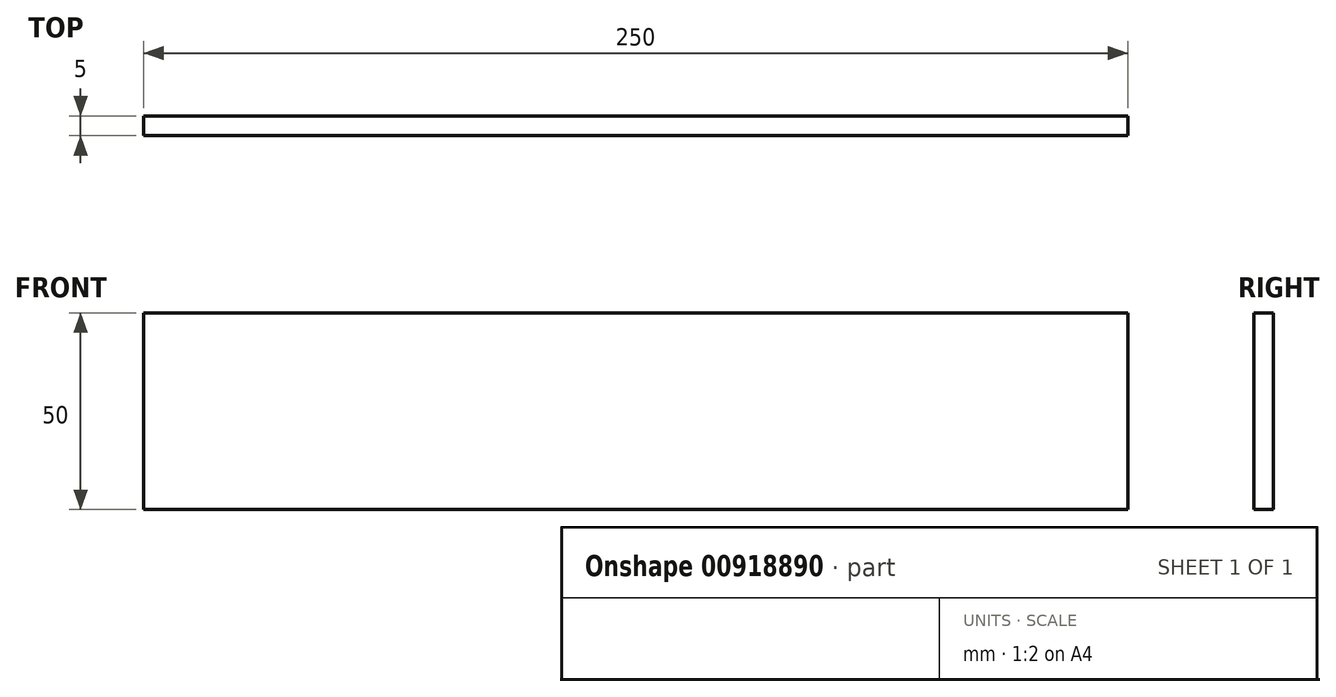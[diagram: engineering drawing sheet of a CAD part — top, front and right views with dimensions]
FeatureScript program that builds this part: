
annotation { "Feature Type Name" : "Feature", "Feature Type Description" : "" }
export const myFeature = defineFeature(function(context is Context, id is Id, definition is map)
    precondition{}
    {
        {
            var Q0;
            Q0=qCreatedBy(makeId("Front.planeOp"),FACE);
            var sketch = newSketch(context, id + "F0", { "sketchPlane" : qUnion([Q0])});
            skLineSegment(sketch, "E0.bottom", {"start": v(-126.8, -42.4) * mm, "end": v(123.2, -42.4) * mm});
            skLineSegment(sketch, "E0.top", {"start": v(-126.8, -92.4) * mm, "end": v(123.2, -92.4) * mm});
            skLineSegment(sketch, "E0.left", {"start": v(-126.8, -42.4) * mm, "end": v(-126.8, -92.4) * mm});
            skLineSegment(sketch, "E0.right", {"start": v(123.2, -42.4) * mm, "end": v(123.2, -92.4) * mm});
            skSolve(sketch);
        }
        {
            var Q0;
            Q0=makeQuery(id+"F0.imprint","IMPRINT",FACE,{"disambiguationData":[TD([[makeQuery(id+"F0.imprint","IMPRINT",EDGE,{"derivedFrom":sQuery(id+"F0.wireOp",EDGE,"E0.bottom")}),-1.0]])]});
            extrude(context, id + "F1", {"entities" : qUnion([Q0]), "depth" : 5 * mm, "offsetDistance" : 25 * mm});
        }
    });
